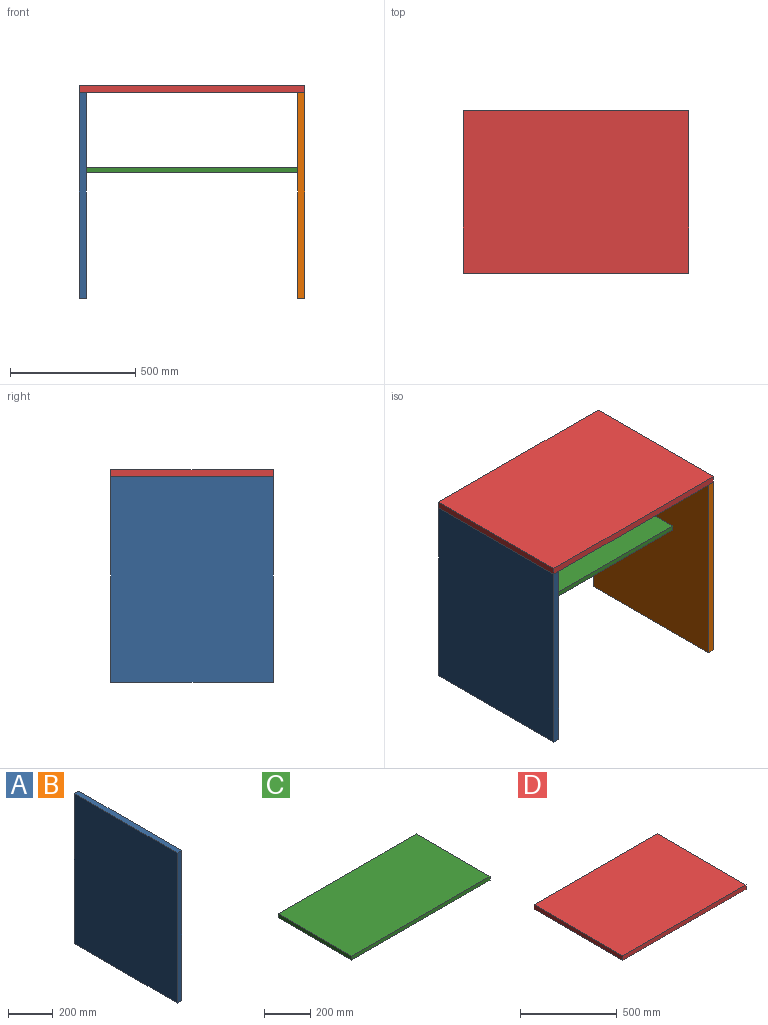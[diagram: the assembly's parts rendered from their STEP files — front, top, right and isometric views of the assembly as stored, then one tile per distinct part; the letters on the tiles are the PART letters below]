
ASSEMBLY  parts=4 mates=3
PART A: 6 faces, bbox 28x650x820 mm
  f0: plane 650x28mm, normal (0,0,-1), area 18200mm2, adj f1,f3,f4,f5
  f1: plane 820x28mm, normal (0,1,0), area 22960mm2, adj f0,f2,f4,f5
  f2: plane 650x28mm, normal (0,0,1), area 18200mm2, adj f1,f3,f4,f5
  f3: plane 820x28mm, normal (0,-1,0), area 22960mm2, adj f0,f2,f4,f5
  f4: plane 820x650mm, normal (1,0,0), area 533000mm2, adj f0,f1,f2,f3
  f5: plane 820x650mm, normal (-1,0,0), area 533000mm2, adj f0,f1,f2,f3
PART B: same geometry as A
PART C: 6 faces, bbox 844x450x20 mm
  f0: plane 844x20mm, normal (0,-1,0), area 16880mm2, adj f1,f3,f4,f5
  f1: plane 450x20mm, normal (1,0,0), area 9000mm2, adj f0,f2,f4,f5
  f2: plane 844x20mm, normal (0,1,0), area 16880mm2, adj f1,f3,f4,f5
  f3: plane 450x20mm, normal (-1,0,0), area 9000mm2, adj f0,f2,f4,f5
  f4: plane 844x450mm, normal (0,0,1), area 379800mm2, adj f0,f1,f2,f3
  f5: plane 844x450mm, normal (0,0,-1), area 379800mm2, adj f0,f1,f2,f3
PART D: 6 faces, bbox 900x650x28 mm
  f0: plane 900x28mm, normal (0,-1,0), area 25200mm2, adj f1,f3,f4,f5
  f1: plane 650x28mm, normal (1,0,0), area 18200mm2, adj f0,f2,f4,f5
  f2: plane 900x28mm, normal (0,1,0), area 25200mm2, adj f1,f3,f4,f5
  f3: plane 650x28mm, normal (-1,0,0), area 18200mm2, adj f0,f2,f4,f5
  f4: plane 900x650mm, normal (0,0,1), area 585000mm2, adj f0,f1,f2,f3
  f5: plane 900x650mm, normal (0,0,-1), area 585000mm2, adj f0,f1,f2,f3
PLACE A t=(0,-325,410)mm
PLACE B t=(872,-325,410)mm
PLACE C t=(450,-225,500)mm
PLACE D t=(450,-325,820)mm
MATE fastened C.f3 <-> A.f4  axis (-1,0,0) through (28,0,500)mm
MATE fastened A.f2 <-> D.f5  axis (0,0,1) through (0,-325,820)mm
MATE fastened B.f2 <-> D.f5  axis (0,0,1) through (900,-325,820)mm
